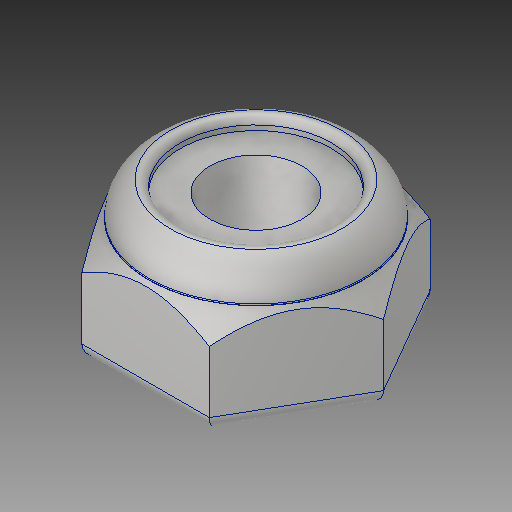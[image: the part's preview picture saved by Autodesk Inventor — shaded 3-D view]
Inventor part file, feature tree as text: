
AUTODESK INVENTOR PART (.ipt)
format: ipt  version: 2017 (Build 210142000, 142)  size: 185,344 bytes
history: native  units: in
note: dims shown in document units (in); Inventor stores cm internally (conversion verified against a paired STEP export)
features: fillet x1
ambient origin geometry x8: Origin, YZ Plane, XZ Plane, XY Plane, X Axis, Y Axis, Z Axis, Center Point
bodies: Solid1 (feature_tree)
feature tree (1):
  fillet  "Fillet5"  [1 undecoded]
note: 1 required parameter value undecoded (feature->parameter linkage not recoverable at this tier; creation-order binding heuristic only, values carry confidence <= 0.55)
